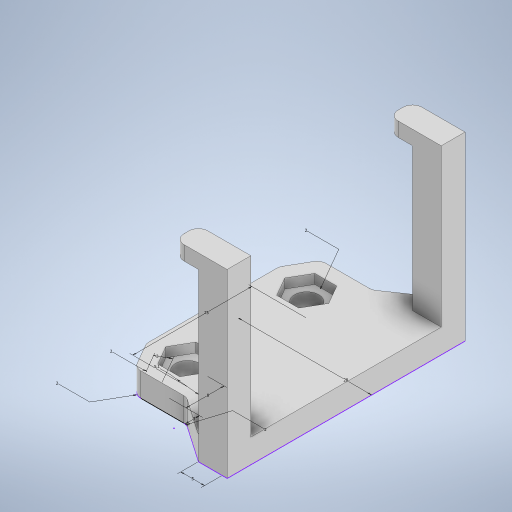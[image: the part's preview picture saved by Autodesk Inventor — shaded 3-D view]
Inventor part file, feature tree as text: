
AUTODESK INVENTOR PART (.ipt)
format: ipt  version: 2024 (Build 280153000, 153)  size: 348,672 bytes
history: native  units: in
note: dims shown in document units (in); Inventor stores cm internally (conversion verified against a paired STEP export)
features: extrude x5, sketch x2
ambient origin geometry x8: Origin, YZ Plane, XZ Plane, XY Plane, X Axis, Y Axis, Z Axis, Center Point
bodies: Solid1 (feature_tree)
feature tree (7):
  sketch  "Sketch2"  dims[d16=1.378in d17=0.0in d18=0.315in]
  extrude  "Extrusion2"  Depth=0.315in
  extrude  "Extrusion4"  Depth=0.1181in
  extrude  "Extrusion6"  Depth=0.1181in
  extrude  "Extrusion7"  Depth=0.1181in TaperAngle=0.0deg
  extrude  "Extrusion8"  Depth=0.9843in
  sketch  "Sketch4"  dims[d19=0.2008in d21=0.1181in d22=0.1181in d25=0.1181in d26=0.0in d27=0.9843in d33=0.1969in d34=0.0787in d35=0.0787in d36=0.0787in d37=0.0787in d38=0.1969in d39=0.0in d40=1.378in d41=0.0in d42=0.3937in d43=0.1969in d44=0.0787in d45=0.1181in d46=0.0in d48=1.1024in d47=0.0197in d49=0.0in d50=0.0in]
